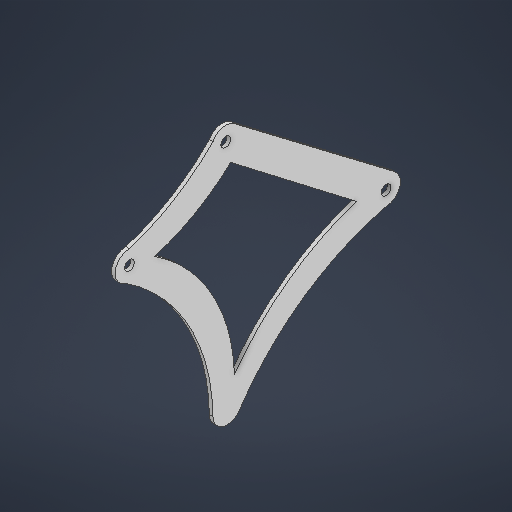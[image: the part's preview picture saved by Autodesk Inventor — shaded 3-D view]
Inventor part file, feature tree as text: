
AUTODESK INVENTOR PART (.ipt)
format: ipt  version: 2025.2 (Build 292293000, 293)  size: 219,648 bytes
history: native  units: in
note: dims shown in document units (in); Inventor stores cm internally (conversion verified against a paired STEP export)
features: extrude x1, sketch x1
ambient origin geometry x8: Origin, YZ Plane, XZ Plane, XY Plane, X Axis, Y Axis, Z Axis, Center Point
bodies: Solid1 (feature_tree)
feature tree (2):
  extrude  "Extrusion1"  Depth=0.0625in TaperAngle=0.0deg
  sketch  "Sketch1"  dims[d0=0.5in d1=0.5in d2=0.5in d3=0.5in d4=0.0625in d5=0.0in]
